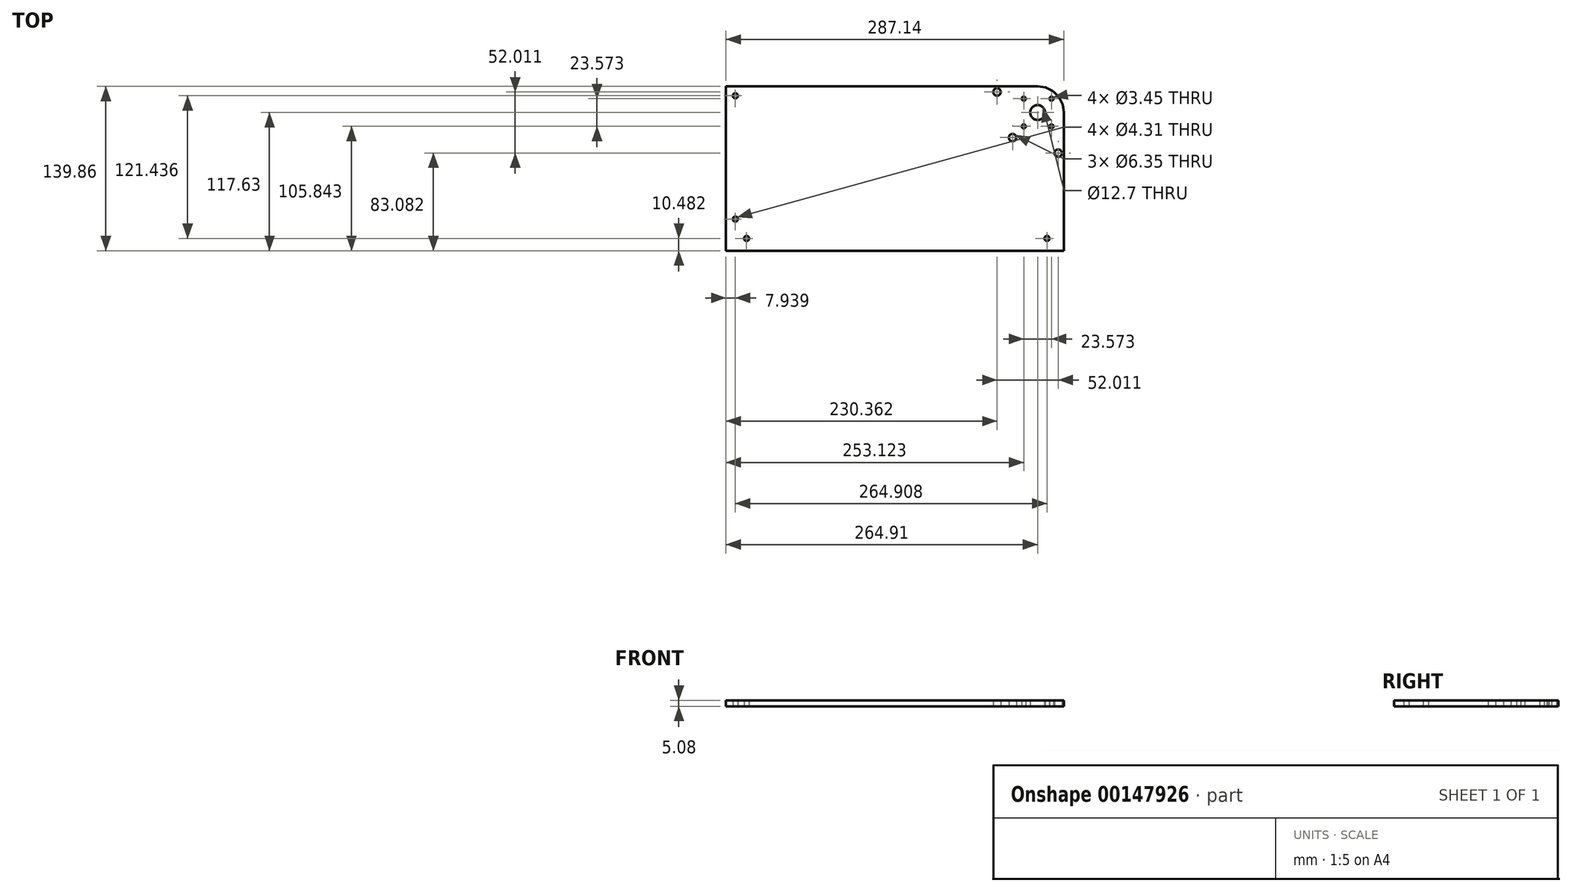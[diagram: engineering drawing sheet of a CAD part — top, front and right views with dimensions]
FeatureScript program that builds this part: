
annotation { "Feature Type Name" : "Feature", "Feature Type Description" : "" }
export const myFeature = defineFeature(function(context is Context, id is Id, definition is map)
    precondition{}
    {
        {
            var Q0;
            Q0=qCreatedBy(makeId("Top.planeOp"),FACE);
            var sketch = newSketch(context, id + "F0", { "sketchPlane" : qUnion([Q0])});
            skCircle(sketch, "E0", {"center": v(-11.79, 11.79) * mm, "radius": 1.73 * mm});
            skCircle(sketch, "E1", {"center": v(11.79, -11.79) * mm, "radius": 1.73 * mm});
            skLineSegment(sketch, "E2.bottom", {"start": v(-264.9, 22.22) * mm, "end": v(0, 22.23) * mm});
            skLineSegment(sketch, "E2.top", {"start": v(-264.9, -117.63) * mm, "end": v(22.23, -117.63) * mm});
            skLineSegment(sketch, "E2.left", {"start": v(-264.9, 22.22) * mm, "end": v(-264.9, -117.63) * mm});
            skPoint(sketch, "E3.middle", {"position": v(0, 0) * mm});
            skCircle(sketch, "E4", {"center": v(11.79, 11.79) * mm, "radius": 1.73 * mm});
            skArc(sketch, "E5", {"start": v(22.23, 0) * mm, "mid": v(15.72, 15.72) * mm, "end": v(0, 22.23) * mm});
            skLineSegment(sketch, "E6", {"start": v(22.23, -117.63) * mm, "end": v(22.23, 0) * mm});
            skLineSegment(sketch, "E7", {"start": v(0, 0) * mm, "end": v(0, -117.63) * mm, "construction": true});
            skLineSegment(sketch, "E8", {"start": v(22.23, -107.15) * mm, "end": v(7.94, -107.15) * mm, "construction": true});
            skCircle(sketch, "E9", {"center": v(7.94, -107.15) * mm, "radius": 2.15 * mm});
            skLineSegment(sketch, "E10", {"start": v(-256.97, 22.22) * mm, "end": v(-256.97, 14.29) * mm, "construction": true});
            skLineSegment(sketch, "E11", {"start": v(-264.9, -107.15) * mm, "end": v(-247.45, -107.15) * mm, "construction": true});
            skCircle(sketch, "E12", {"center": v(-247.45, -107.15) * mm, "radius": 2.15 * mm});
            skCircle(sketch, "E13", {"center": v(-256.97, 14.29) * mm, "radius": 2.15 * mm});
            skLineSegment(sketch, "E14", {"start": v(-256.97, -90.64) * mm, "end": v(-256.97, 14.29) * mm, "construction": true});
            skLineSegment(sketch, "E15", {"start": v(-256.97, -90.64) * mm, "end": v(-256.97, -107.15) * mm, "construction": true});
            skCircle(sketch, "E16", {"center": v(-256.97, -90.64) * mm, "radius": 2.15 * mm});
            skCircle(sketch, "E17", {"center": v(0, 0) * mm, "radius": 6.35 * mm});
            skCircle(sketch, "E18", {"center": v(11.79, 11.79) * mm, "radius": 5.56 * mm, "construction": true});
            skLineSegment(sketch, "E19", {"start": v(-256.97, 14.29) * mm, "end": v(-264.9, 14.29) * mm, "construction": true});
            skLineSegment(sketch, "E20", {"start": v(7.94, -107.15) * mm, "end": v(7.94, -117.63) * mm, "construction": true});
            skLineSegment(sketch, "E21", {"start": v(0, 0) * mm, "end": v(17.46, -34.55) * mm, "construction": true});
            skLineSegment(sketch, "E22", {"start": v(0, 0) * mm, "end": v(-34.55, 17.46) * mm, "construction": true});
            skLineSegment(sketch, "E23", {"start": v(0, 0) * mm, "end": v(-21.33, -21.33) * mm, "construction": true});
            skCircle(sketch, "E24", {"center": v(17.46, -34.55) * mm, "radius": 4.76 * mm, "construction": true});
            skLineSegment(sketch, "E25", {"start": v(17.46, -34.55) * mm, "end": v(-21.33, -21.33) * mm, "construction": true});
            skLineSegment(sketch, "E26", {"start": v(-21.33, -21.33) * mm, "end": v(-34.55, 17.46) * mm, "construction": true});
            skCircle(sketch, "E27", {"center": v(-34.55, 17.46) * mm, "radius": 3.18 * mm});
            skCircle(sketch, "E28", {"center": v(17.46, -34.55) * mm, "radius": 3.18 * mm});
            skCircle(sketch, "E29", {"center": v(-21.33, -21.33) * mm, "radius": 3.18 * mm});
            skLineSegment(sketch, "E30.bottom", {"start": v(11.79, 11.79) * mm, "end": v(-11.79, 11.79) * mm, "construction": true});
            skLineSegment(sketch, "E30.top", {"start": v(11.79, -11.79) * mm, "end": v(-11.79, -11.79) * mm, "construction": true});
            skLineSegment(sketch, "E30.left", {"start": v(11.79, 11.79) * mm, "end": v(11.79, -11.79) * mm, "construction": true});
            skLineSegment(sketch, "E30.right", {"start": v(-11.79, 11.79) * mm, "end": v(-11.79, -11.79) * mm, "construction": true});
            skCircle(sketch, "E31", {"center": v(-11.79, -11.79) * mm, "radius": 1.73 * mm});
            skSolve(sketch);
        }
        {
            var Q0;
            Q0=qSketchRegion(id+"F0",true);
            extrude(context, id + "F1", {"entities" : qUnion([Q0]), "depth" : 5.08 * mm});
        }
    });
